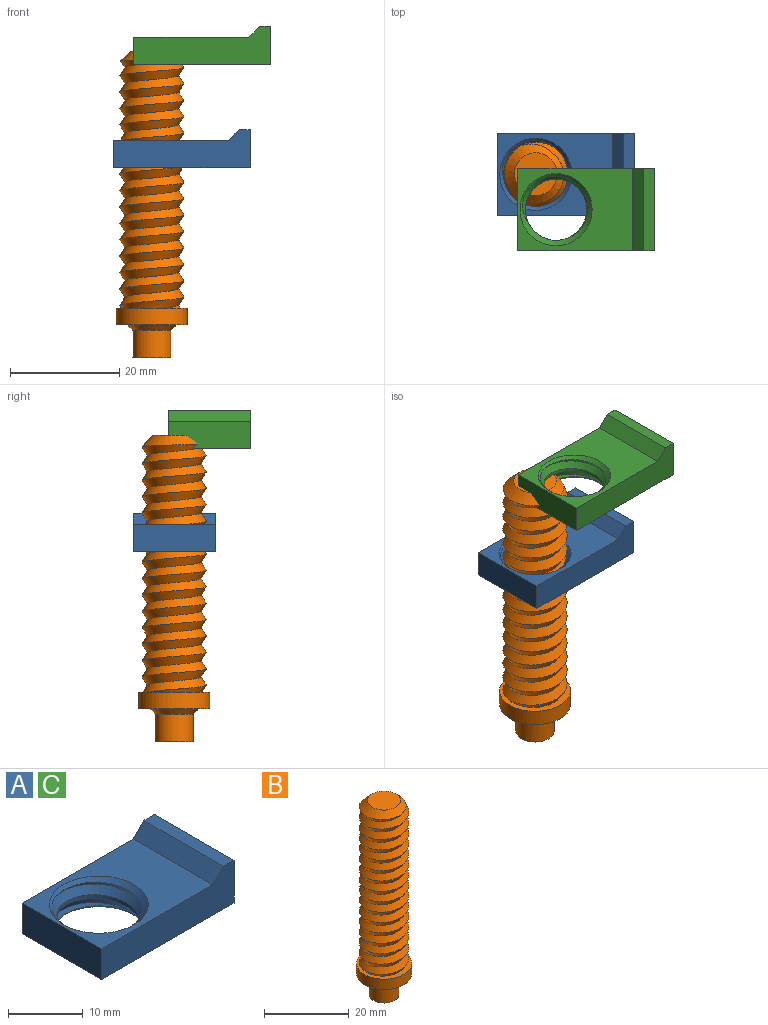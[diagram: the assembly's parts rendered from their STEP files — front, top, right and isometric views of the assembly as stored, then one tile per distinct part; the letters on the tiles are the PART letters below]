
ASSEMBLY  parts=3 mates=1
PART A: 13 faces, bbox 25x15x8.6 mm
  f0: cylinder r=5.6mm len=11.2mm, axis (0,0,-1), area 21.7mm2, adj f1,f2,f8,f9
  f1: cone r=6.6mm half-angle=45deg, axis (0,0,-1), area 38.3mm2, adj f0,f7,f8,f9
  f2: cone r=5.6mm half-angle=45deg, axis (0,0,1), area 38.4mm2, adj f0,f6,f8,f9
  f3: plane 25x7mm, normal (0,1,0), area 131mm2, adj f4,f6,f7,f10,f11,f12
  f4: plane 15x5mm, normal (-1,0,0), area 75mm2, adj f3,f5,f6,f7
  f5: plane 25x7mm, normal (0,-1,0), area 131mm2, adj f4,f6,f7,f10,f11,f12
  f6: plane 21x15mm, normal (0,0,1), area 178.2mm2, adj f2,f3,f4,f5,f12
  f7: plane 25x15mm, normal (0,0,-1), area 238.2mm2, adj f1,f3,f4,f5,f10
  f8: bspline ~14.71x12.74mm, area 67.2mm2, adj f0,f1,f2,f9
  f9: bspline ~14.71x12.74mm, area 67.3mm2, adj f0,f1,f2,f8
  f10: plane 15x7mm, normal (1,0,0), area 105mm2, adj f3,f5,f7,f11
  f11: plane 15x2mm, normal (0,0,1), area 30mm2, adj f3,f5,f10,f12
  f12: plane 15x2mm, normal (-0.71,0,0.71), area 42.4mm2, adj f3,f5,f6,f11
PART B: 12 faces, bbox 13x13.6x56.6 mm
  f0: plane 7.8x7.8mm, normal (0,0,1), area 47.8mm2, adj f1
  f1: cone r=3.9mm half-angle=45deg, axis (0,0,-1), area 61.6mm2, adj f0,f3,f5
  f2: plane 0.06x0.05mm, normal (-0.87,-0.5,0), area 0mm2, adj f4,f5,f7
  f3: bspline ~48.5x13.55mm, area 915mm2, adj f1,f4,f5,f7
  f4: bspline ~0.6x0.33mm, area 0mm2, adj f2,f3,f7
  f5: bspline ~49x13.55mm, area 919.9mm2, adj f1,f2,f3,f7
  f6: cylinder r=6.5mm len=13mm, axis (0,0,-1), area 122.5mm2, adj f7,f8
  f7: plane 13x13mm, normal (0,0,1), area 41.4mm2, adj f2,f3,f4,f5,f6
  f8: plane 13x13mm, normal (0,0,-1), area 69.1mm2, adj f6,f11
  f9: cylinder r=3.5mm len=7mm, axis (0,0,1), area 110mm2, adj f10,f11
  f10: plane 7x7mm, normal (0,0,-1), area 38.5mm2, adj f9
  f11: cone r=4.5mm half-angle=45deg, axis (0,0,1), area 35.5mm2, adj f8,f9
PART C: same geometry as A
PLACE A t=(-3.7,6.5,-18.85)mm
PLACE B t=(-3.7,6.5,-47.53)mm
PLACE C at identity
MATE slider B.f1 <-> A.f0  axis (0,0,-1) through (-3.7,6.5,2.47)mm
